# Revit family: 2GAHP-AR
name_source: partatom
category: Wyposażenie mechaniczne
revit_build: Autodesk Revit 2015 (Build: 20160512_1515(x64)
units: mm (PartAtom-declared; Revit-internal decimal feet)

## types (2) — shared parameters
Autor = www.archispace.pl
Ciśnienie gazu zasilającego (LPG G30/G31) = 32 - 42 mbar
Ciśnienie gazu zasilającego (gaz ziemny G20) = 17 - 23 mbar
Dokumentacja techniczna = http://www.gazuno.pl
Głębokość = 1230 mm  [stored 4.03543 ft]
IP = X5D
Ilość wody w urządzeniu = 3.0 L
Klasyfikacja obciążenia = Inne
Maksymalne ciśnienie robocze = 4 pasek
Materiał obudowa 1 = Robur_CashmereGrey
Materiał obudowa 2 = Robur_Czarny
Materiał podstawa = Robur_Stal
Max. ciśnienie w układzie absorpcyjnym = 35 bar
Max. przepływ wody grzewczej = 1.389 L/s
Max. temperatura powietrza zewnętrznego (tryb chłodzenia) = 45 °C
Max. temperatura powietrza zewnętrznego (tryb grzania) = 35 °C
Max. temperatura wody na wejściu do urządzenia (dla ogrzewania) = 50 °C
Max. temperatura wody na wyjściu z urządzenia = 60 °C
Min. przepływ wody grzewczej = 0.389 L/s
Min. temperatura powietrza zewnętrznego (tryb chłodzenia) = 0 °C
Min. temperatura powietrza zewnętrznego (tryb grzania) = -20 °C
Min. temperatura wody na wejściu do urządzenia (podczas pracy ciągłej) = 20 °C
Napięcie zasilania = 230 V
Nominalna moc grzewcza palnika = 25700 W
Nominalna temperatura powietrza zewnętrznego (tryb chłodzenia) = 35 °C
Nominalny przepływ wody grzewczej = 0.844 L/s
Nominalny spadek ciśnienia wody grzewczej = 0.29 pasek
Opis = Absorpcyjna pompa ciepła typu powietrze-woda do celów grzewczych i klimatyzacji do średnich i dużych kubatur. Zasilana gazem i energią odnawialną.
Producent = Robur
Rzeczywista moc grzewcza palnika = 25200 W
Sposób instalacji = B23, B35
Szerokość = 850 mm  [stored 2.78871 ft]
URL = www.gazuno.pl
Współczynnik mocy = 1
Wysokość = 1545 mm

## per-type parameters (varying)
| type | Ciśnienie akustyczne w odległości 5 metrów | Moc elektryczna | Obciążenie pozorne | S1 | STD | Waga | Wysokość bez uwzględnienia komina |
| GAHP-AR | 57,6 dB (A) | 840 W | 840 VA | Nie | Tak | 380.00 kg | 1445 mm |
| GAHP-AR S | 53 dB (A) | 870 W | 870 VA | Tak | Nie | 390.00 kg | 1545 mm |

note: column(s) folded — value = type name in every type: Model

note: [stored X ft] marks values corroborated as IEEE doubles in the binary element streams (Revit-internal decimal feet)
